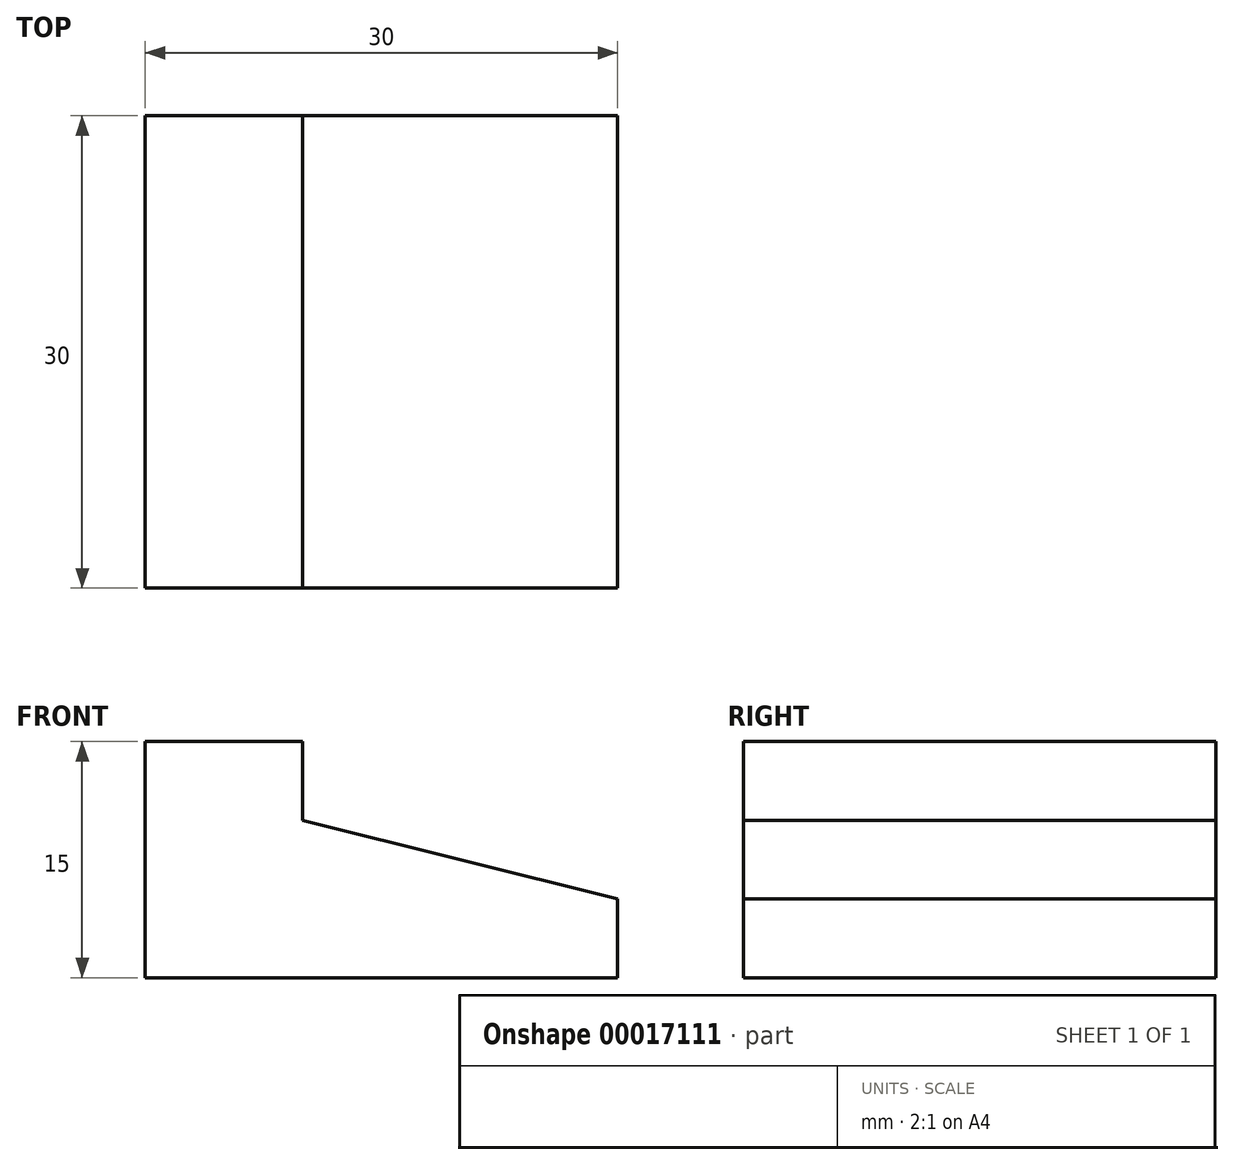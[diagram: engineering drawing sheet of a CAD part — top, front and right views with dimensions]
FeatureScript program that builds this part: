
annotation { "Feature Type Name" : "Feature", "Feature Type Description" : "" }
export const myFeature = defineFeature(function(context is Context, id is Id, definition is map)
    precondition{}
    {
        {
            var Q0;
            Q0=qCreatedBy(makeId("Front.planeOp"),FACE);
            var sketch = newSketch(context, id + "F0", { "sketchPlane" : qUnion([Q0])});
            skLineSegment(sketch, "E0", {"start": v(-30.86, 28) * mm, "end": v(-30.86, 13) * mm});
            skLineSegment(sketch, "E1", {"start": v(-30.86, 13) * mm, "end": v(-0.86, 13) * mm});
            skLineSegment(sketch, "E2", {"start": v(-0.86, 13) * mm, "end": v(-0.86, 18) * mm});
            skLineSegment(sketch, "E3", {"start": v(-0.86, 18) * mm, "end": v(-20.86, 23) * mm});
            skLineSegment(sketch, "E4", {"start": v(-20.86, 23) * mm, "end": v(-20.86, 28) * mm});
            skLineSegment(sketch, "E5", {"start": v(-20.86, 28) * mm, "end": v(-30.86, 28) * mm});
            skSolve(sketch);
        }
        {
            var Q0;
            Q0 = qSketchRegion(id + "F0", true);
            extrude(context, id + "F1", {"entities" : qUnion([Q0]), "depth" : 30 * mm});
        }
    });
